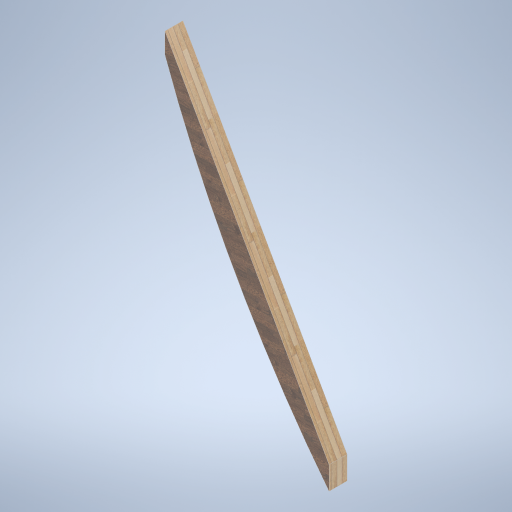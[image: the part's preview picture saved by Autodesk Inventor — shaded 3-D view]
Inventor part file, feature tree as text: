
AUTODESK INVENTOR PART (.ipt)
format: ipt  version: 2024.2 (Build 282272000, 272)  size: 296,960 bytes
history: native  units: mm
features: extrude x1, sketch x1
ambient origin geometry x8: Origin, YZ Plane, XZ Plane, XY Plane, X Axis, Y Axis, Z Axis, Center Point
bodies: Body1 (feature_tree)
feature tree (2):
  extrude  "Extrusion2"  Depth=200.0mm TaperAngle=0.0deg
  sketch  "Sketch1"  dims[d3=12000.0mm d4=200.0mm d5=0.0mm]
